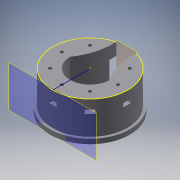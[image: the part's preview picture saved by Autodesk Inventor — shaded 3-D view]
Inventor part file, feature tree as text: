
AUTODESK INVENTOR PART (.ipt)
format: ipt  version: 2017 (Build 210142000, 142)  size: 276,480 bytes
history: native  units: mm
features: sketch x8, extrude x7, plane x2, pattern_circular x1
ambient origin geometry x8: Origin, YZ Plane, XZ Plane, XY Plane, X Axis, Y Axis, Z Axis, Center Point
bodies: Body1 (feature_tree)
feature tree (18):
  extrude  "Extrusion6"  Depth=21.0mm
  extrude  "Extrusion12"  Depth=5.0mm
  extrude  "Extrusion13"  Depth=10.0mm
  extrude  "Extrusion14"  Depth=3.0mm
  sketch  "Sketch12"  dims[d80=5.0mm d81=6.0mm]
  plane  "Work Plane2"
  extrude  "Extrusion15"  Depth=5.0mm
  pattern_circular  "Circular Pattern2"  [2 undecoded]
  plane  "Work Plane3"
  extrude  "Extrusion16"  Depth=5.0mm
  extrude  "Extrusion17"  Depth=5.0mm
  sketch  "Sketch1"  dims[d1=42.0mm d28=21.0mm]
  sketch  "Sketch9"  dims[d29=5.0mm d30=0.0mm d39=60.0mm]
  sketch  "Sketch10"  dims[d76=10.0mm d77=10.5mm]
  sketch  "Sketch11"  dims[d78=85.0mm d79=3.0mm]
  sketch  "Sketch13"  dims[d82=5.0mm]
  sketch  "Sketch14"  dims[d83=6.0mm]
  sketch  "Sketch15"  dims[d84=10.0mm d85=0.0mm d86=7.5mm d87=79.81228mm d88=7.5mm d89=35.0mm d90=0.0mm d91=30.0mm d92=3.5mm d93=80.0mm d95=360.0deg d97=35.0mm d98=0.0mm d99=10.0mm d100=4.0mm d101=4.0mm d102=8.0mm d103=15.0mm d104=0.0mm d105=80.0mm d106=360.0deg d109=2.0mm d111=20.0mm d112=90.0deg d113=10.0mm d114=20.0mm d115=7.5mm d116=0.0mm d118=3.0mm d119=3.0mm d120=5.0mm d121=0.0mm]
note: 2 required parameter values undecoded (feature->parameter linkage not recoverable at this tier; creation-order binding heuristic only, values carry confidence <= 0.55)
